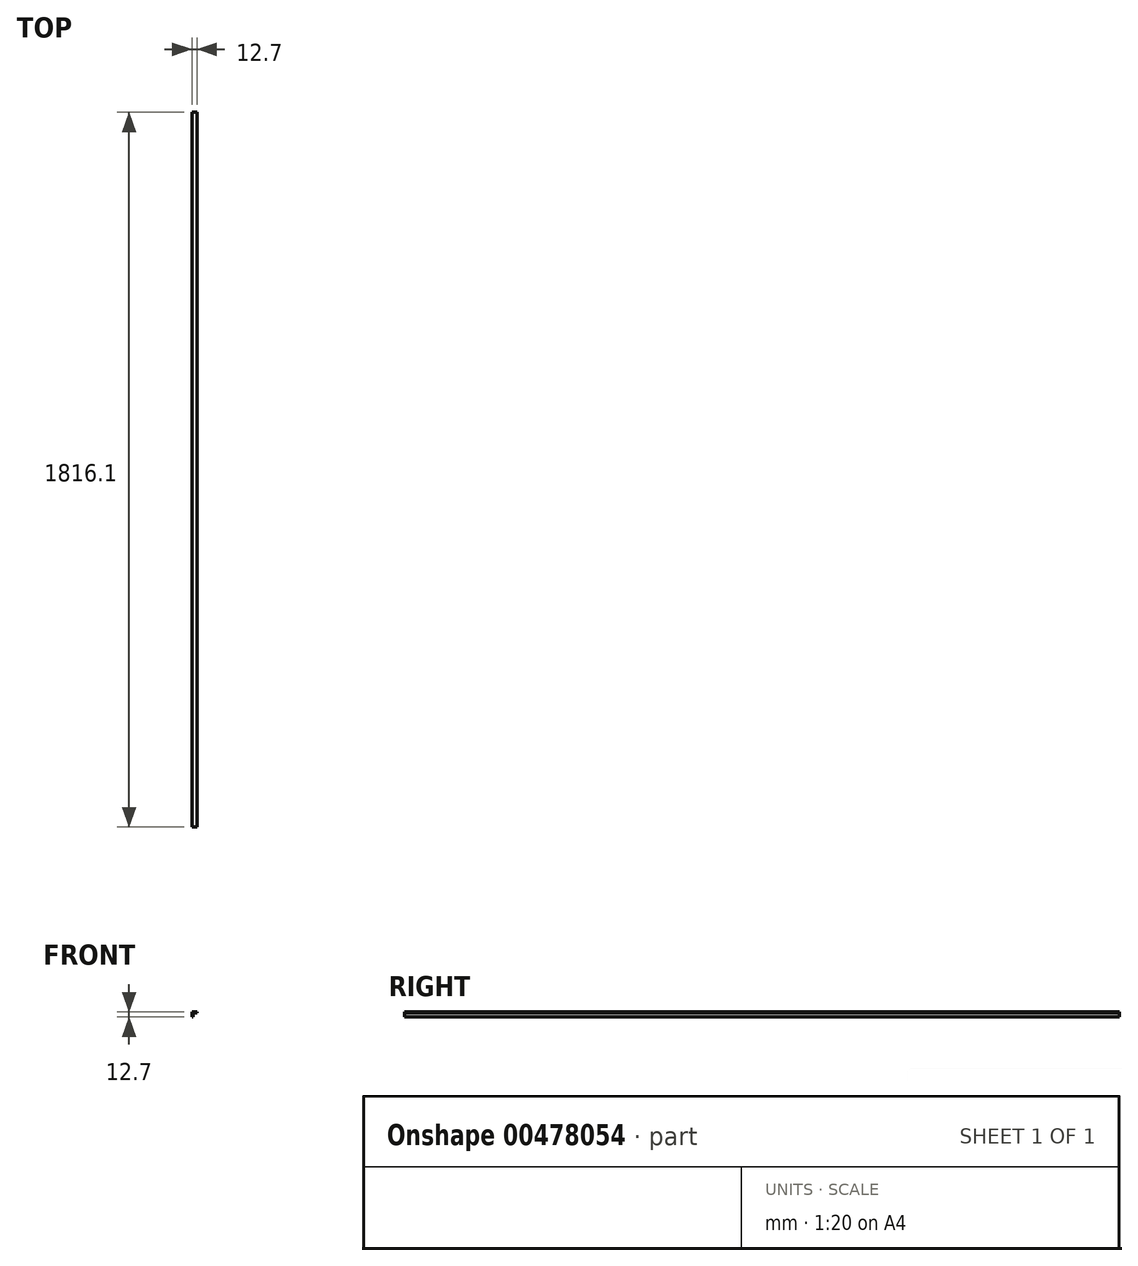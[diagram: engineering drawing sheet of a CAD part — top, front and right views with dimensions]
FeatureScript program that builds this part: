
annotation { "Feature Type Name" : "Feature", "Feature Type Description" : "" }
export const myFeature = defineFeature(function(context is Context, id is Id, definition is map)
    precondition{}
    {
        {
            var Q0;
            Q0=qCreatedBy(makeId("Front.planeOp"),FACE);
            var sketch = newSketch(context, id + "F0", { "sketchPlane" : qUnion([Q0])});
            skLineSegment(sketch, "E0.bottom", {"start": v(-66.98, 44.7) * mm, "end": v(-64.31, 44.7) * mm});
            skLineSegment(sketch, "E0.top", {"start": v(-66.98, 32) * mm, "end": v(-64.31, 32) * mm});
            skLineSegment(sketch, "E0.left", {"start": v(-66.98, 44.7) * mm, "end": v(-66.98, 32) * mm});
            skLineSegment(sketch, "E0.right", {"start": v(-64.31, 42.04) * mm, "end": v(-64.31, 32) * mm});
            skLineSegment(sketch, "E1.bottom", {"start": v(-64.31, 44.7) * mm, "end": v(-54.28, 44.7) * mm});
            skLineSegment(sketch, "E1.top", {"start": v(-64.31, 42.04) * mm, "end": v(-54.28, 42.04) * mm});
            skLineSegment(sketch, "E1.right", {"start": v(-54.28, 44.7) * mm, "end": v(-54.28, 42.04) * mm});
            skSolve(sketch);
        }
        {
            var Q0;
            Q0=makeQuery(id+"F0.imprint","IMPRINT",FACE,{"disambiguationData":[TD([[makeQuery(id+"F0.imprint","IMPRINT",EDGE,{"derivedFrom":sQuery(id+"F0.wireOp",EDGE,"E0.bottom")}),-1.0]])]});
            extrude(context, id + "F1", {"entities" : qUnion([Q0]), "depth" : 1816.1 * mm});
        }
    });
